# Revit family: 1447xxx Nagoya
name_source: partatom
category: Lighting Fixtures
units: mm (PartAtom-declared; Revit-internal decimal feet)

## family parameters
Always vertical = Yes
Cut with Voids When Loaded = No
Host = Wall
Light Source = No
Maintain Annotation Orientation = No
OmniClass Number = 23.80.70.00
OmniClass Title = Lighting
Part Type = Normal
Room Calculation Point = No
Round Connector Dimension = Use Diameter
Shared = No

## types (2) — shared parameters
Dimmable = No
Driver Required = No
Lamp = LED
Light Source Fixed = No
Main Finish = Various
Main Material = Metal - Zinc
Manufacturer = Astro Lighting Ltd
Manufacturer URL - Europe and Rest of World = www.astrolighting.com
Manufacturer URL - North America = us.astrolighting.com
Power (Watts) = Lamp Dependent
Product Dimensions (MM) = 250 x 250-345 x 138-309
Product Location = Bathroom Indoor
Product Name = Nagoya
Product Weight (KG) = 2.7
URL = www.astrolighting.com
zero-valued in all types: Default Elevation, Electrical Class

## per-type parameters (varying)
| type | ADA compliant | Dimming Method | Driver Included | Efficacy (lm/w) | Length of Cable Supplied | Location / IP Rating | Product SKU |
| CE | N / A |  |  | Lamp Dependent |  | IP44 | 1447001 |
| ETL |  | Not Applicable | Not Applicable | Lamp Dependent (lm/W) | Not Applicable | Not Applicable | 1447003 |

## geometry (parser evidence)
native form markers: Sweep x3
no freeform markers — native parametric forms only
